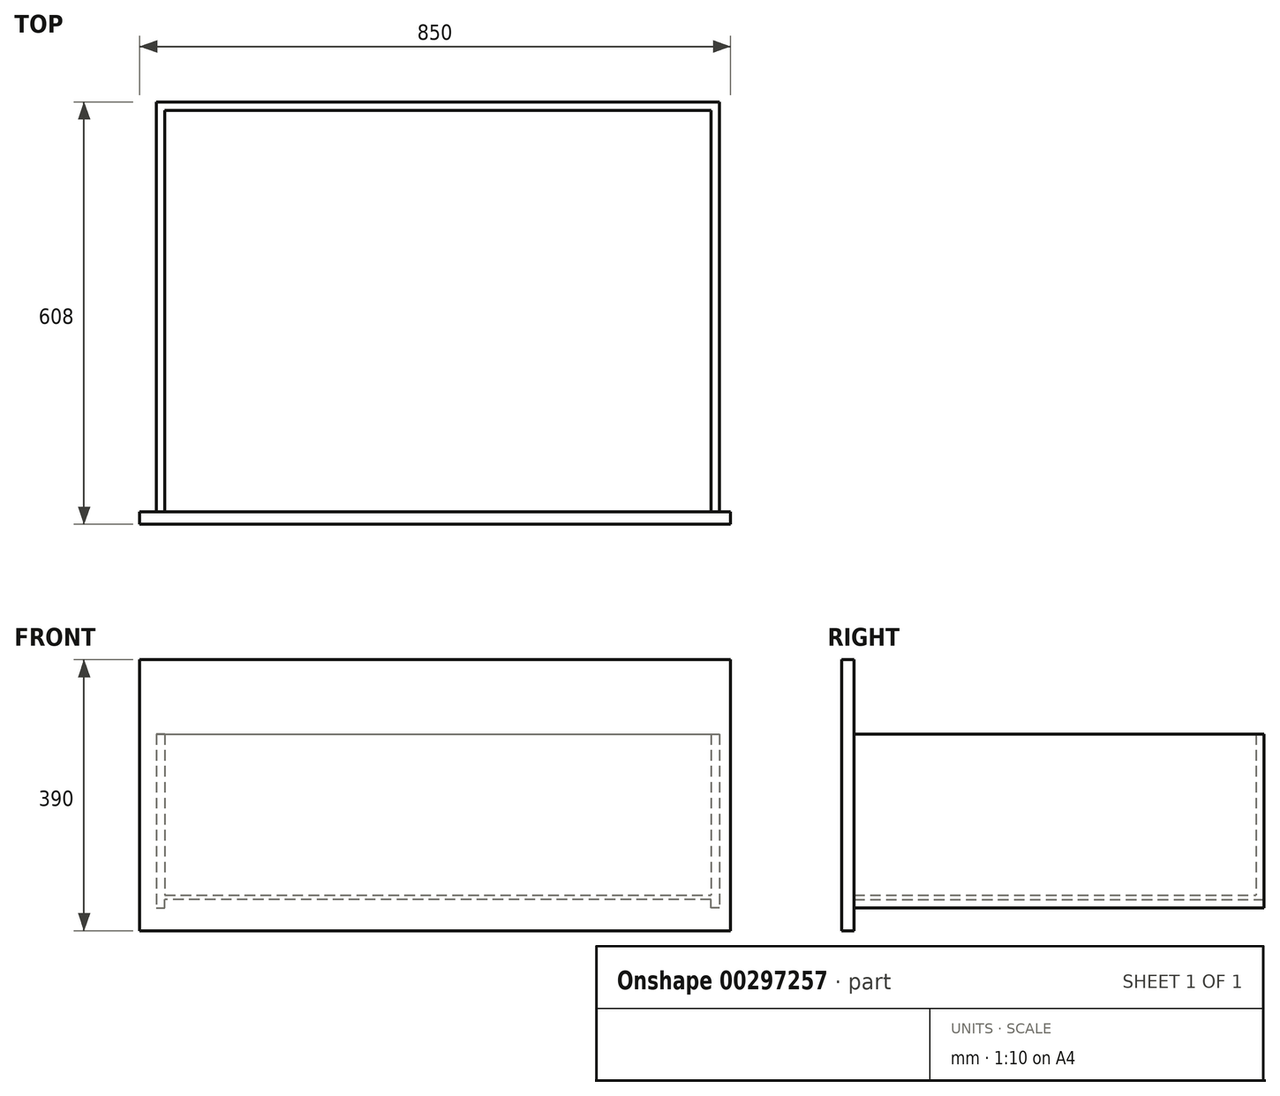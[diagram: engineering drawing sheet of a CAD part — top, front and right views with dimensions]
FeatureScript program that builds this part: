
annotation { "Feature Type Name" : "Feature", "Feature Type Description" : "" }
export const myFeature = defineFeature(function(context is Context, id is Id, definition is map)
    precondition{}
    {
        {
            var Q0;
            Q0=qCreatedBy(makeId("Front.planeOp"),FACE);
            var sketch = newSketch(context, id + "F0", { "sketchPlane" : qUnion([Q0])});
            skLineSegment(sketch, "E0.bottom", {"start": v(393, -3) * mm, "end": v(-393, -3) * mm});
            skLineSegment(sketch, "E0.top", {"start": v(393, 3) * mm, "end": v(-393, 3) * mm});
            skPoint(sketch, "E0.middle", {"position": v(0, 0) * mm});
            skLineSegment(sketch, "E1", {"start": v(-393, 3) * mm, "end": v(-393, 235) * mm});
            skLineSegment(sketch, "E2", {"start": v(-393, 235) * mm, "end": v(-405, 235) * mm});
            skLineSegment(sketch, "E3", {"start": v(-405, 235) * mm, "end": v(-405, -15) * mm});
            skLineSegment(sketch, "E4", {"start": v(-405, -15) * mm, "end": v(-393, -15) * mm});
            skLineSegment(sketch, "E5", {"start": v(-393, -15) * mm, "end": v(-393, -3) * mm});
            skLineSegment(sketch, "E6", {"start": v(393, 3) * mm, "end": v(393, 235) * mm});
            skLineSegment(sketch, "E7", {"start": v(393, 235) * mm, "end": v(405, 235) * mm});
            skLineSegment(sketch, "E8", {"start": v(405, 235) * mm, "end": v(405, -15) * mm});
            skLineSegment(sketch, "E9", {"start": v(405, -15) * mm, "end": v(393, -15) * mm});
            skLineSegment(sketch, "E10", {"start": v(393, -15) * mm, "end": v(393, -3) * mm});
            skSolve(sketch);
        }
        {
            var Q0;
            Q0=qSketchRegion(id+"F0",true);
            extrude(context, id + "F1", {"entities" : qUnion([Q0]), "depth" : 590 * mm});
        }
        {
            var Q0;
            Q0=makeQuery(id+"F1.opExtrude","SWEPT_FACE",FACE,{"disambiguationData":[OSD([sQuery(id+"F0.wireOp",EDGE,"E6")])]});
            var sketch = newSketch(context, id + "F2", { "sketchPlane" : qUnion([Q0])});
            skLineSegment(sketch, "E11.bottom", {"start": v(0, 235) * mm, "end": v(12, 235) * mm});
            skLineSegment(sketch, "E11.top", {"start": v(0, 3) * mm, "end": v(12, 3) * mm});
            skLineSegment(sketch, "E11.left", {"start": v(0, 235) * mm, "end": v(0, 3) * mm});
            skLineSegment(sketch, "E11.right", {"start": v(12, 235) * mm, "end": v(12, 3) * mm});
            skSolve(sketch);
        }
        {
            var Q0;
            Q0=qSketchRegion(id+"F2",true);
            extrude(context, id + "F3", {"entities" : qUnion([Q0]), "operationType" : NewBodyOperationType.ADD, "depth" : 786 * mm});
        }
        {
            var Q0;
            Q0=makeQuery(id+"F1.opExtrude","CAP_FACE",FACE,{"disambiguationData":[OSD([sQuery(id+"F0.wireOp",EDGE,"E0.bottom"),sQuery(id+"F0.wireOp",EDGE,"E0.top"),sQuery(id+"F0.wireOp",EDGE,"E1"),sQuery(id+"F0.wireOp",EDGE,"E2"),sQuery(id+"F0.wireOp",EDGE,"E3"),sQuery(id+"F0.wireOp",EDGE,"E4"),sQuery(id+"F0.wireOp",EDGE,"E5"),sQuery(id+"F0.wireOp",EDGE,"E6"),sQuery(id+"F0.wireOp",EDGE,"E7"),sQuery(id+"F0.wireOp",EDGE,"E8"),sQuery(id+"F0.wireOp",EDGE,"E9"),sQuery(id+"F0.wireOp",EDGE,"E10")])],"isStart":false});
            var sketch = newSketch(context, id + "F4", { "sketchPlane" : qUnion([Q0])});
            skLineSegment(sketch, "E12.bottom", {"start": v(-429, 342) * mm, "end": v(421, 342) * mm});
            skLineSegment(sketch, "E12.top", {"start": v(-429, -48) * mm, "end": v(421, -48) * mm});
            skLineSegment(sketch, "E12.left", {"start": v(-429, 342) * mm, "end": v(-429, -48) * mm});
            skLineSegment(sketch, "E12.right", {"start": v(421, 342) * mm, "end": v(421, -48) * mm});
            skSolve(sketch);
        }
        {
            var Q0;
            Q0=qSketchRegion(id+"F4",true);
            extrude(context, id + "F5", {"entities" : qUnion([Q0]), "operationType" : NewBodyOperationType.ADD, "depth" : 18 * mm});
        }
    });
